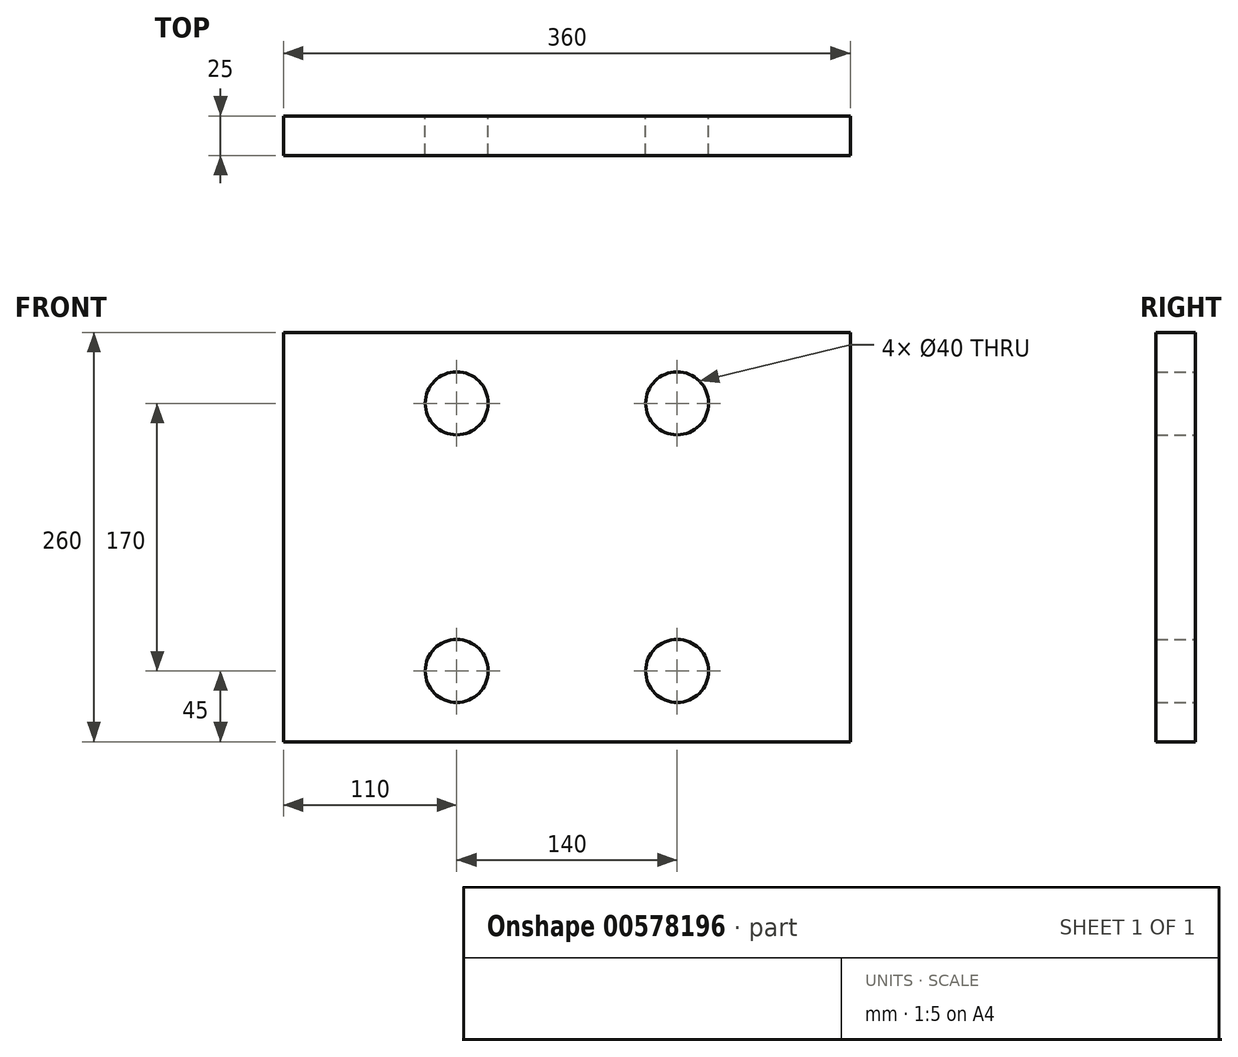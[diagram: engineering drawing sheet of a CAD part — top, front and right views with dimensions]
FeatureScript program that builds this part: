
annotation { "Feature Type Name" : "Feature", "Feature Type Description" : "" }
export const myFeature = defineFeature(function(context is Context, id is Id, definition is map)
    precondition{}
    {
        {
            var Q0;
            Q0=qCreatedBy(makeId("Front.planeOp"),FACE);
            var sketch = newSketch(context, id + "F0", { "sketchPlane" : qUnion([Q0])});
            skLineSegment(sketch, "E0.bottom", {"start": v(-180, 130) * mm, "end": v(180, 130) * mm});
            skLineSegment(sketch, "E0.top", {"start": v(-180, -130) * mm, "end": v(180, -130) * mm});
            skLineSegment(sketch, "E0.left", {"start": v(-180, 130) * mm, "end": v(-180, -130) * mm});
            skLineSegment(sketch, "E0.right", {"start": v(180, 130) * mm, "end": v(180, -130) * mm});
            skLineSegment(sketch, "E1.bottom", {"start": v(-70, 85) * mm, "end": v(70, 85) * mm, "construction": true});
            skLineSegment(sketch, "E1.top", {"start": v(-70, -85) * mm, "end": v(70, -85) * mm, "construction": true});
            skLineSegment(sketch, "E1.left", {"start": v(-70, 85) * mm, "end": v(-70, -85) * mm, "construction": true});
            skLineSegment(sketch, "E1.right", {"start": v(70, 85) * mm, "end": v(70, -85) * mm, "construction": true});
            skCircle(sketch, "E2", {"center": v(-70, 85) * mm, "radius": 20 * mm});
            skCircle(sketch, "E3", {"center": v(70, 85) * mm, "radius": 20 * mm});
            skCircle(sketch, "E4", {"center": v(-70, -85) * mm, "radius": 20 * mm});
            skCircle(sketch, "E5", {"center": v(70, -85) * mm, "radius": 20 * mm});
            skSolve(sketch);
        }
        {
            var Q0;
            Q0=makeQuery(id+"F0.imprint","IMPRINT",FACE,{"disambiguationData":[TD([[makeQuery(id+"F0.imprint","IMPRINT",EDGE,{"derivedFrom":sQuery(id+"F0.wireOp",EDGE,"E0.bottom")}),-1.0]])]});
            extrude(context, id + "F1", {"entities" : qUnion([Q0]), "depth" : 25 * mm, "offsetDistance" : 25 * mm});
        }
    });
